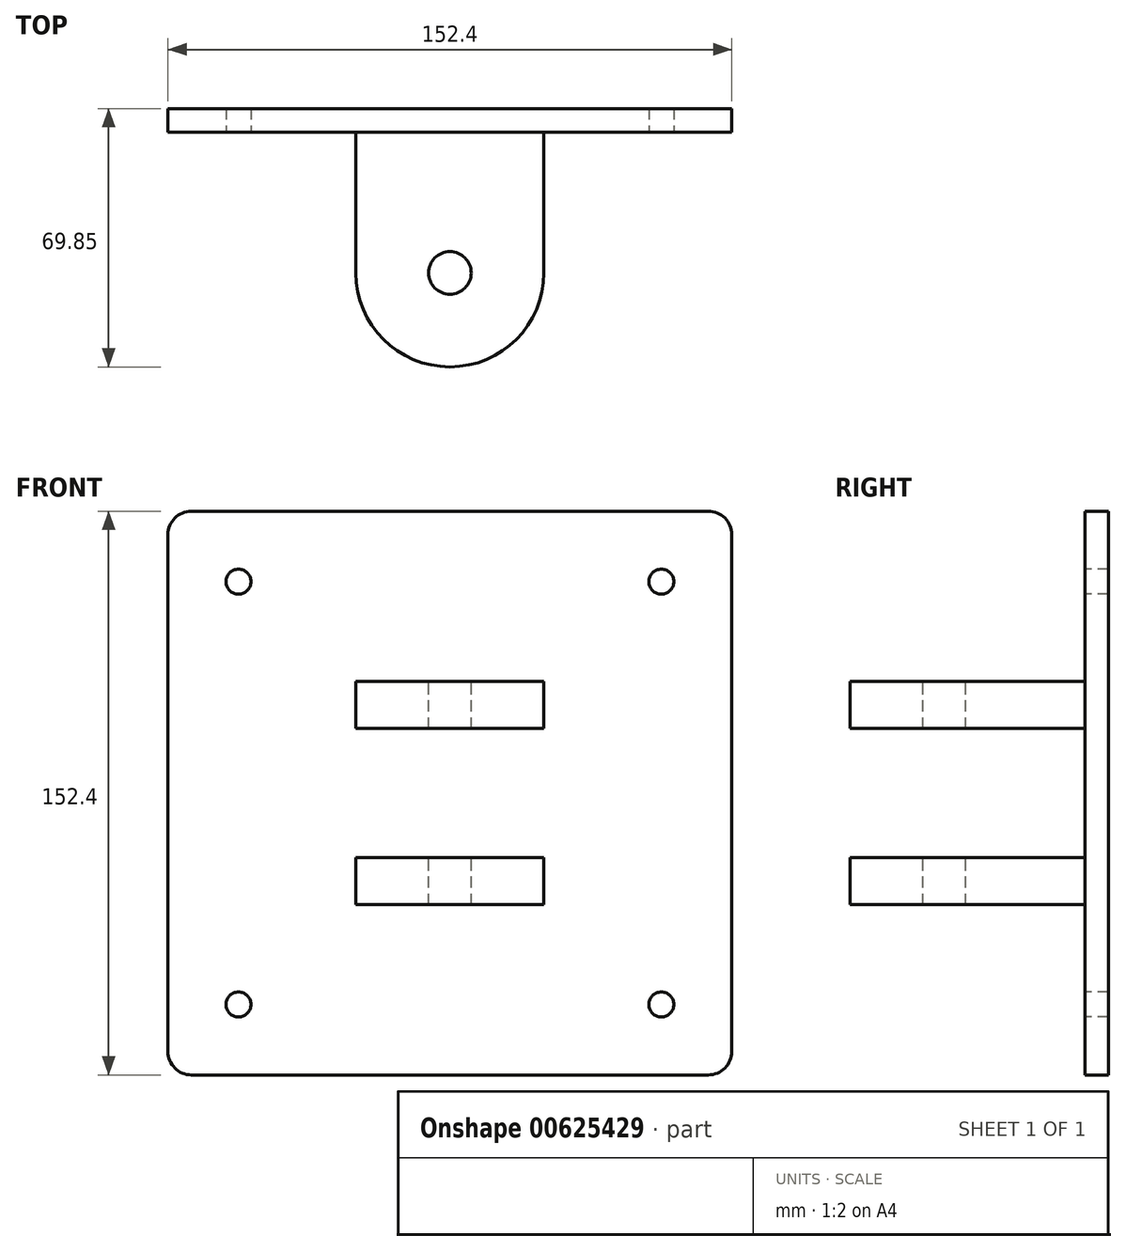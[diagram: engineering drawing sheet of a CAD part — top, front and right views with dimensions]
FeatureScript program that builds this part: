
annotation { "Feature Type Name" : "Feature", "Feature Type Description" : "" }
export const myFeature = defineFeature(function(context is Context, id is Id, definition is map)
    precondition{}
    {
        {
            var Q0;
            Q0=qCreatedBy(makeId("Front.planeOp"),FACE);
            var sketch = newSketch(context, id + "F0", { "sketchPlane" : qUnion([Q0])});
            skLineSegment(sketch, "E0.bottom", {"start": v(0, 0) * mm, "end": v(152.4, 0) * mm});
            skLineSegment(sketch, "E0.top", {"start": v(0, 152.4) * mm, "end": v(152.4, 152.4) * mm});
            skLineSegment(sketch, "E0.left", {"start": v(0, 0) * mm, "end": v(0, 152.4) * mm});
            skLineSegment(sketch, "E0.right", {"start": v(152.4, 0) * mm, "end": v(152.4, 152.4) * mm});
            skSolve(sketch);
        }
        {
            var Q0;
            Q0 = qSketchRegion(id + "F0", true);
            extrude(context, id + "F1", {"entities" : qUnion([Q0]), "depth" : 6.35 * mm, "offsetDistance" : 25.4 * mm});
        }
        {
            var Q0;
            Q0=makeQuery(id+"F1.opExtrude","CAP_FACE",FACE,{"disambiguationData":[OSD([sQuery(id+"F0.wireOp",EDGE,"E0.bottom"),sQuery(id+"F0.wireOp",EDGE,"E0.top"),sQuery(id+"F0.wireOp",EDGE,"E0.left"),sQuery(id+"F0.wireOp",EDGE,"E0.right")])],"isStart":false});
            var sketch = newSketch(context, id + "F2", { "sketchPlane" : qUnion([Q0])});
            skLineSegment(sketch, "E1.bottom", {"start": v(50.8, 93.66) * mm, "end": v(101.6, 93.66) * mm});
            skLineSegment(sketch, "E1.top", {"start": v(50.8, 106.36) * mm, "end": v(101.6, 106.36) * mm});
            skLineSegment(sketch, "E1.left", {"start": v(50.8, 93.66) * mm, "end": v(50.8, 106.36) * mm});
            skLineSegment(sketch, "E1.right", {"start": v(101.6, 93.66) * mm, "end": v(101.6, 106.36) * mm});
            skLineSegment(sketch, "E2.bottom", {"start": v(50.8, 46.04) * mm, "end": v(101.6, 46.04) * mm});
            skLineSegment(sketch, "E2.top", {"start": v(50.8, 58.74) * mm, "end": v(101.6, 58.74) * mm});
            skLineSegment(sketch, "E2.left", {"start": v(50.8, 46.04) * mm, "end": v(50.8, 58.74) * mm});
            skLineSegment(sketch, "E2.right", {"start": v(101.6, 46.04) * mm, "end": v(101.6, 58.74) * mm});
            skSolve(sketch);
        }
        {
            var Q0;
            Q0 = qSketchRegion(id + "F2", true);
            extrude(context, id + "F3", {"entities" : qUnion([Q0]), "depth" : 63.5 * mm, "offsetDistance" : 25.4 * mm});
        }
        {
            var Q0;
            Q0=makeQuery(id+"F3.opExtrude","SWEPT_FACE",FACE,{"disambiguationData":[OSD([sQuery(id+"F2.wireOp",EDGE,"E1.top")])]});
            var sketch = newSketch(context, id + "F4", { "sketchPlane" : qUnion([Q0])});
            skCircle(sketch, "E3", {"center": v(76.2, -44.45) * mm, "radius": 5.75 * mm});
            skSolve(sketch);
        }
        {
            var Q0;
            Q0 = qSketchRegion(id + "F4", true);
            extrude(context, id + "F5", {"entities" : qUnion([Q0]), "operationType" : NewBodyOperationType.REMOVE, "oppositeDirection" : true, "depth" : 76.2 * mm, "offsetDistance" : 25.4 * mm});
        }
        {
            var Q0;
            Q0=makeQuery(id+"F1.opExtrude","CAP_FACE",FACE,{"disambiguationData":[OSD([sQuery(id+"F0.wireOp",EDGE,"E0.bottom"),sQuery(id+"F0.wireOp",EDGE,"E0.top"),sQuery(id+"F0.wireOp",EDGE,"E0.left"),sQuery(id+"F0.wireOp",EDGE,"E0.right")])],"isStart":false});
            var sketch = newSketch(context, id + "F6", { "sketchPlane" : qUnion([Q0])});
            skCircle(sketch, "E4", {"center": v(19.05, 133.35) * mm, "radius": 3.37 * mm});
            skLineSegment(sketch, "E5", {"start": v(152.4, 76.2) * mm, "end": v(0, 76.2) * mm});
            skLineSegment(sketch, "E6", {"start": v(76.2, 152.4) * mm, "end": v(76.2, 0) * mm});
            skCircle(sketch, "E7.MirrorC", {"center": v(133.35, 133.35) * mm, "radius": 3.37 * mm});
            skCircle(sketch, "E8.MirrorC", {"center": v(19.05, 19.05) * mm, "radius": 3.37 * mm});
            skCircle(sketch, "E9.MirrorC", {"center": v(133.35, 19.05) * mm, "radius": 3.37 * mm});
            skSolve(sketch);
        }
        {
            var Q0;
            Q0 = qSketchRegion(id + "F6", true);
            extrude(context, id + "F7", {"entities" : qUnion([Q0]), "operationType" : NewBodyOperationType.REMOVE, "oppositeDirection" : true, "depth" : 6.35 * mm, "offsetDistance" : 25.4 * mm});
        }
        {
            var Q0;
            Q0=makeQuery(id+"F3.opExtrude","CAP_EDGE",EDGE,{"disambiguationData":[OSD([sQuery(id+"F2.wireOp",EDGE,"E1.left")])],"isStart":false});
            var Q1;
            Q1=makeQuery(id+"F3.opExtrude","CAP_EDGE",EDGE,{"disambiguationData":[OSD([sQuery(id+"F2.wireOp",EDGE,"E1.right")])],"isStart":false});
            var Q2;
            Q2=makeQuery(id+"F3.opExtrude","CAP_EDGE",EDGE,{"disambiguationData":[OSD([sQuery(id+"F2.wireOp",EDGE,"E2.left")])],"isStart":false});
            var Q3;
            Q3=makeQuery(id+"F3.opExtrude","CAP_EDGE",EDGE,{"disambiguationData":[OSD([sQuery(id+"F2.wireOp",EDGE,"E2.right")])],"isStart":false});
            fillet(context, id + "F8", {"entities" : qUnion([Q0, Q1, Q2, Q3]), "radius" : 25.4 * mm, "tangentPropagation" : true, "allowEdgeOverflow" : false});
        }
        {
            var Q0;
            Q0=makeQuery(id+"F1.opExtrude","SWEPT_EDGE",EDGE,{"disambiguationData":[OSD([sQuery(id+"F0.wireOp",EDGE,"E0.top"),sQuery(id+"F0.wireOp",EDGE,"E0.left")])]});
            var Q1;
            Q1=makeQuery(id+"F1.opExtrude","SWEPT_EDGE",EDGE,{"disambiguationData":[OSD([sQuery(id+"F0.wireOp",EDGE,"E0.top"),sQuery(id+"F0.wireOp",EDGE,"E0.right")])]});
            var Q2;
            Q2=makeQuery(id+"F1.opExtrude","SWEPT_EDGE",EDGE,{"disambiguationData":[OSD([sQuery(id+"F0.wireOp",EDGE,"E0.bottom"),sQuery(id+"F0.wireOp",EDGE,"E0.left")])]});
            var Q3;
            Q3=makeQuery(id+"F1.opExtrude","SWEPT_EDGE",EDGE,{"disambiguationData":[OSD([sQuery(id+"F0.wireOp",EDGE,"E0.bottom"),sQuery(id+"F0.wireOp",EDGE,"E0.right")])]});
            fillet(context, id + "F9", {"entities" : qUnion([Q0, Q1, Q2, Q3]), "radius" : 6.35 * mm, "tangentPropagation" : true, "allowEdgeOverflow" : false});
        }
    });
